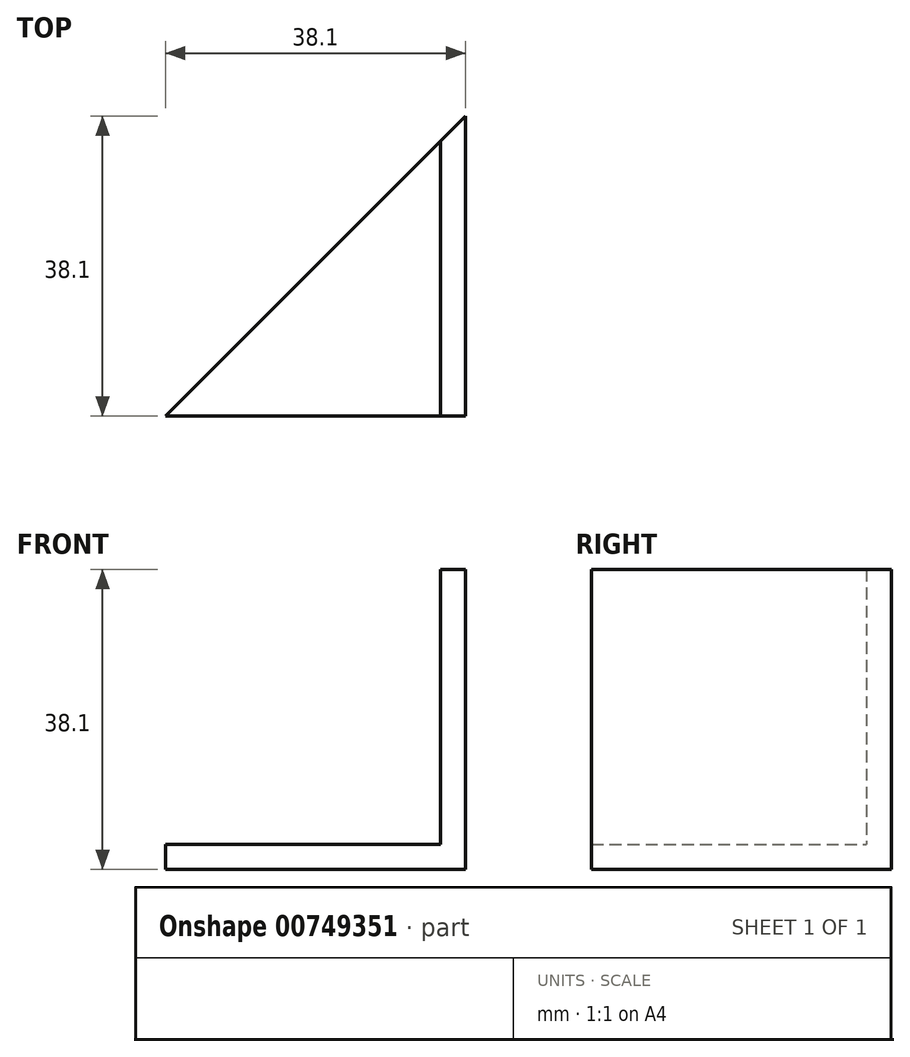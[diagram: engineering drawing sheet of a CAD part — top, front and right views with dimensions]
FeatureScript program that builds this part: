
annotation { "Feature Type Name" : "Feature", "Feature Type Description" : "" }
export const myFeature = defineFeature(function(context is Context, id is Id, definition is map)
    precondition{}
    {
        {
            var Q0;
            Q0=qCreatedBy(makeId("Front.planeOp"),FACE);
            var sketch = newSketch(context, id + "F0", { "sketchPlane" : qUnion([Q0])});
            skLineSegment(sketch, "E0", {"start": v(0, 0) * mm, "end": v(38.1, 0) * mm});
            skLineSegment(sketch, "E1", {"start": v(38.1, 0) * mm, "end": v(38.1, 38.1) * mm});
            skLineSegment(sketch, "E2", {"start": v(38.1, 38.1) * mm, "end": v(34.93, 38.1) * mm});
            skLineSegment(sketch, "E3", {"start": v(34.93, 38.1) * mm, "end": v(34.93, 3.18) * mm});
            skLineSegment(sketch, "E4", {"start": v(34.93, 3.18) * mm, "end": v(0, 3.18) * mm});
            skLineSegment(sketch, "E5", {"start": v(0, 3.18) * mm, "end": v(0, 0) * mm});
            skSolve(sketch);
        }
        {
            var Q0;
            Q0=makeQuery(id+"F0.imprint","IMPRINT",FACE,{"disambiguationData":[TD([[makeQuery(id+"F0.imprint","IMPRINT",EDGE,{"derivedFrom":sQuery(id+"F0.wireOp",EDGE,"E0")}),1.0]])]});
            extrude(context, id + "F1", {"entities" : qUnion([Q0]), "depth" : 76.2 * mm, "offsetDistance" : 25.4 * mm});
        }
        {
            var Q0;
            Q0=makeQuery(id+"F1.opExtrude","SWEPT_FACE",FACE,{"disambiguationData":[OSD([sQuery(id+"F0.wireOp",EDGE,"E2")])]});
            var sketch = newSketch(context, id + "F2", { "sketchPlane" : qUnion([Q0])});
            skLineSegment(sketch, "E6.0.0", {"start": v(34.93, 0) * mm, "end": v(0, 0) * mm});
            skLineSegment(sketch, "E6.0.1", {"start": v(0, 0) * mm, "end": v(0, -76.2) * mm});
            skLineSegment(sketch, "E6.0.2", {"start": v(0, -76.2) * mm, "end": v(34.93, -76.2) * mm});
            skLineSegment(sketch, "E6.0.3", {"start": v(34.93, -76.2) * mm, "end": v(34.93, 0) * mm});
            skLineSegment(sketch, "E7.0.0", {"start": v(38.1, 0) * mm, "end": v(34.93, 0) * mm});
            skLineSegment(sketch, "E7.0.1", {"start": v(34.93, 0) * mm, "end": v(34.93, -76.2) * mm});
            skLineSegment(sketch, "E7.0.2", {"start": v(34.93, -76.2) * mm, "end": v(38.1, -76.2) * mm});
            skLineSegment(sketch, "E7.0.3", {"start": v(38.1, -76.2) * mm, "end": v(38.1, 0) * mm});
            skLineSegment(sketch, "E8", {"start": v(0, -76.2) * mm, "end": v(38.1, -38.1) * mm});
            skSolve(sketch);
        }
        {
            var Q0;
            {var subQ5=sQuery(id+"F2.wireOp",EDGE,"jwPPydwL-I8nz-FAQ8-x2R8-Dw9Q3XHQzeYP");Q0=makeQuery(id+"F2.imprint","IMPRINT",FACE,{"disambiguationData":[TD([[makeQuery(id+"F2.imprint","IMPRINT",EDGE,{"derivedFrom":subQ5}),-1.0]])]});}
            var Q1;
            {var subQ5=sQuery(id+"F2.wireOp",EDGE,"e2RgZvDG-ba0k-fZ9I-BLuU-SAfyZTGH9uWr");Q1=makeQuery(id+"F2.imprint","IMPRINT",FACE,{"disambiguationData":[TD([[makeQuery(id+"F2.imprint","IMPRINT",EDGE,{"derivedFrom":subQ5}),1.0]])]});}
            var Q2;
            {var subQ0=sQuery(id+"F2.wireOp",EDGE,"E6.0.0");Q2=makeQuery(id+"F2.imprint","IMPRINT",FACE,{"disambiguationData":[TD([[makeQuery(id+"F2.imprint","IMPRINT",EDGE,{"derivedFrom":subQ0}),1.0]])]});}
            var Q3;
            {var subQ0=sQuery(id+"F2.wireOp",EDGE,"E7.0.0");Q3=makeQuery(id+"F2.imprint","IMPRINT",FACE,{"disambiguationData":[TD([[makeQuery(id+"F2.imprint","IMPRINT",EDGE,{"derivedFrom":subQ0}),1.0]])]});}
            extrude(context, id + "F3", {"entities" : qUnion([Q0, Q1, Q2, Q3]), "operationType" : NewBodyOperationType.REMOVE, "endBound" : BoundingType.THROUGH_ALL, "oppositeDirection" : true, "depth" : 25.4 * mm, "offsetDistance" : 25.4 * mm});
        }
    });
